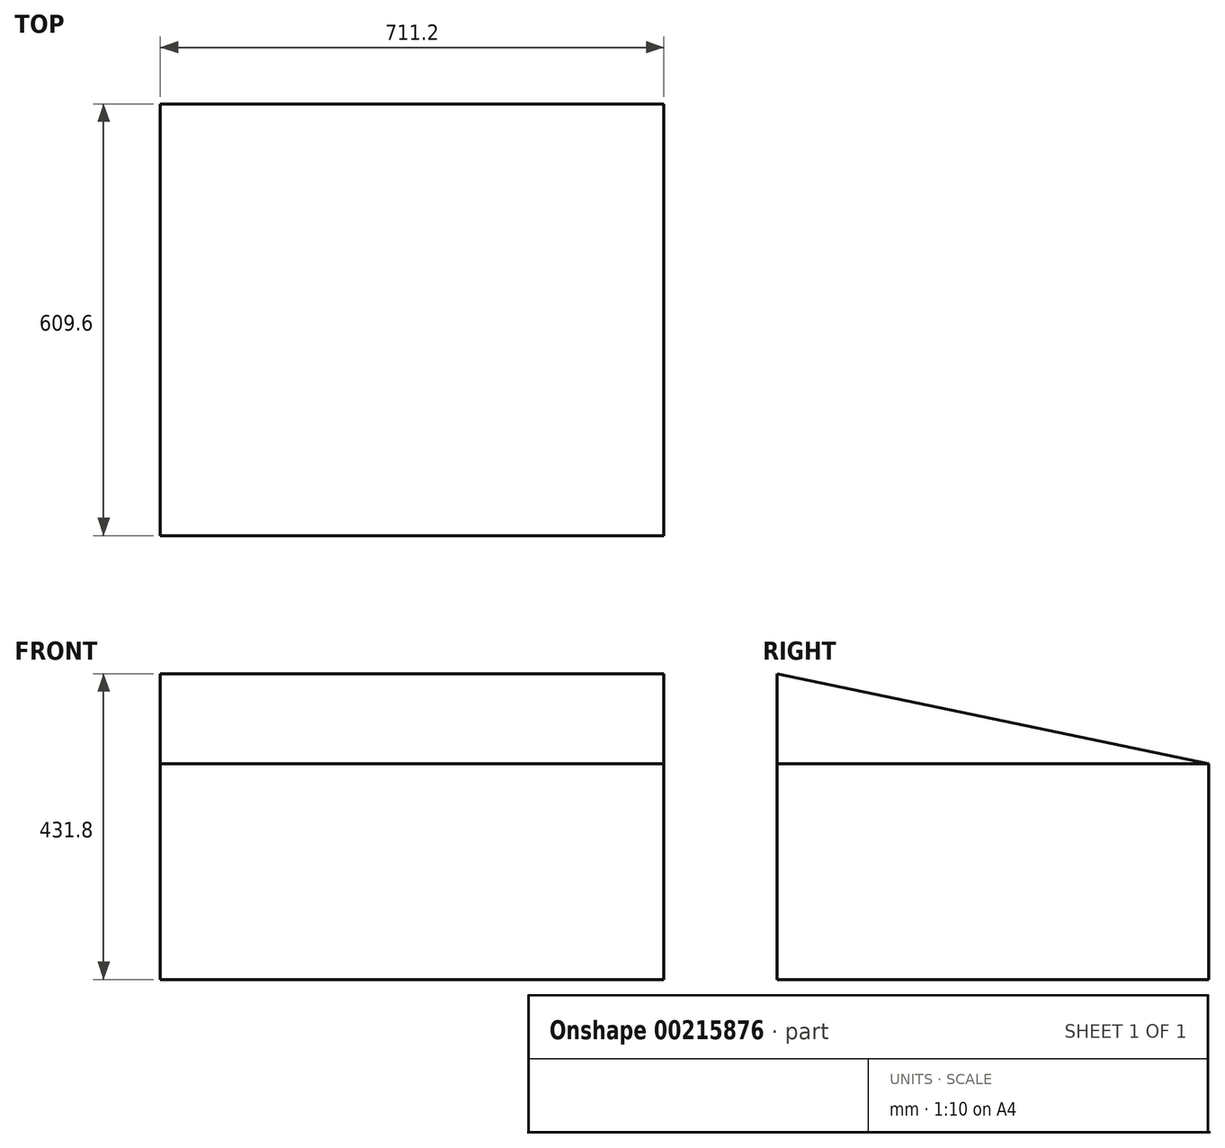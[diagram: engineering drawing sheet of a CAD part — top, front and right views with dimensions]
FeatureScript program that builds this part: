
annotation { "Feature Type Name" : "Feature", "Feature Type Description" : "" }
export const myFeature = defineFeature(function(context is Context, id is Id, definition is map)
    precondition{}
    {
        {
            var Q0;
            Q0=qCreatedBy(makeId("Top.planeOp"),FACE);
            var sketch = newSketch(context, id + "F0", { "sketchPlane" : qUnion([Q0])});
            skLineSegment(sketch, "E0.bottom", {"start": v(355.6, 304.8) * mm, "end": v(-355.6, 304.8) * mm});
            skLineSegment(sketch, "E0.top", {"start": v(355.6, -304.8) * mm, "end": v(-355.6, -304.8) * mm});
            skLineSegment(sketch, "E0.left", {"start": v(355.6, 304.8) * mm, "end": v(355.6, -304.8) * mm});
            skLineSegment(sketch, "E0.right", {"start": v(-355.6, 304.8) * mm, "end": v(-355.6, -304.8) * mm});
            skPoint(sketch, "E0.middle", {"position": v(0, 0) * mm});
            skSolve(sketch);
        }
        {
            var Q0;
            Q0 = qSketchRegion(id + "F0", true);
            extrude(context, id + "F1", {"entities" : qUnion([Q0]), "depth" : 304.8 * mm});
        }
        {
            var Q0;
            Q0=makeQuery(id+"F1.opExtrude","SWEPT_FACE",FACE,{"disambiguationData":[OSD([sQuery(id+"F0.wireOp",EDGE,"E0.right")])]});
            var sketch = newSketch(context, id + "F2", { "sketchPlane" : qUnion([Q0])});
            skLineSegment(sketch, "E1", {"start": v(-304.8, 304.8) * mm, "end": v(304.8, 431.8) * mm});
            skLineSegment(sketch, "E2", {"start": v(304.8, 304.8) * mm, "end": v(-304.8, 304.8) * mm});
            skLineSegment(sketch, "E3", {"start": v(304.8, 304.8) * mm, "end": v(304.8, 431.8) * mm});
            skSolve(sketch);
        }
        {
            var Q0;
            Q0 = qSketchRegion(id + "F2", true);
            extrude(context, id + "F3", {"entities" : qUnion([Q0]), "oppositeDirection" : true, "depth" : 711.2 * mm});
        }
    });
